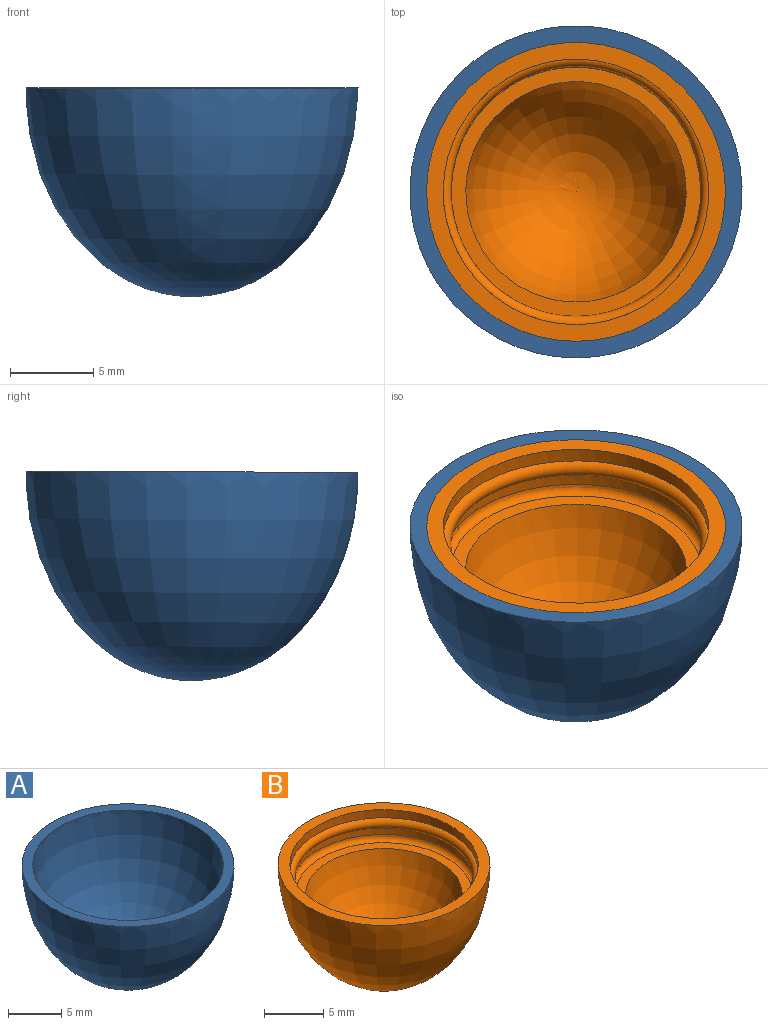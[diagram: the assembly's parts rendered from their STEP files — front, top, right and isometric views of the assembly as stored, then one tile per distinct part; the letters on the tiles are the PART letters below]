
ASSEMBLY  parts=2 mates=1
PART A: 3 faces, bbox 19.9x19.9x12.6 mm
  f0: revolved ~17.93x17.93mm, area 606.5mm2, adj f1
  f1: cone r=8.97mm half-angle=89.7deg, axis (0,0,1), area 59.5mm2, adj f0,f2
  f2: revolved ~19.93x19.93mm, area 737.3mm2, adj f1
PART B: 8 faces, bbox 18x18x11.5 mm
  f0: torus R=7.98mm, axis (0,0,1), area 74mm2, adj f1
  f1: cone r=7.97mm half-angle=0.2deg, axis (0,0,-1), area 40.6mm2, adj f0,f2
  f2: cone r=8.97mm half-angle=89.7deg, axis (0,0,1), area 53.2mm2, adj f1,f3
  f3: revolved ~17.93x17.93mm, area 606.5mm2, adj f2
  f4: cone r=7.97mm half-angle=0.2deg, axis (0,0,-1), area 39.2mm2, adj f5
  f5: torus R=7.47mm, axis (0,0,1), area 38.4mm2, adj f4,f6
  f6: cone r=7.47mm half-angle=89.8deg, axis (0,0,1), area 38.1mm2, adj f5
  f7: revolved ~13.22x6.61mm, area 0mm2
PLACE A t=(-4.64,-7.72,-11.05)mm
PLACE B t=(-4.64,-7.72,-11.05)mm
MATE fastened B.f1 <-> A.f1  axis (0,0,1) through (-4.64,-7.73,-19.31)mm
